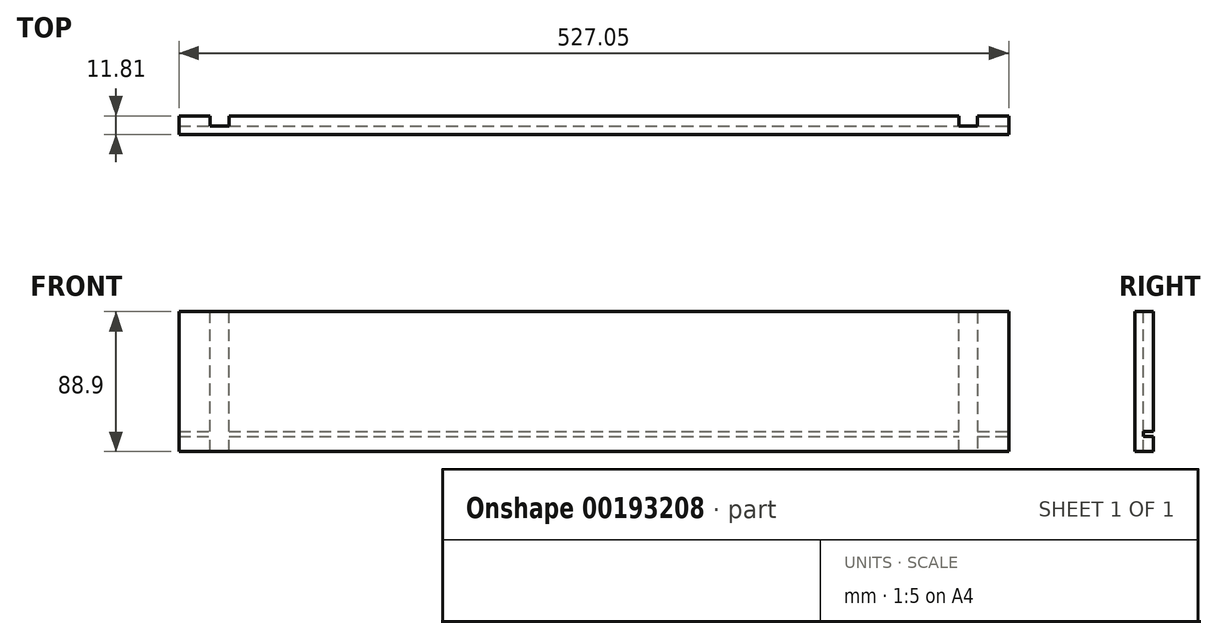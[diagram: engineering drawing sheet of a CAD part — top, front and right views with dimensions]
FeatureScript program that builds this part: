
annotation { "Feature Type Name" : "Feature", "Feature Type Description" : "" }
export const myFeature = defineFeature(function(context is Context, id is Id, definition is map)
    precondition{}
    {
        {
            var Q0;
            Q0=qCreatedBy(makeId("Right.planeOp"),FACE);
            var sketch = newSketch(context, id + "F0", { "sketchPlane" : qUnion([Q0])});
            skLineSegment(sketch, "E0.MirrorCS", {"start": v(12.46, -79.46) * mm, "end": v(12.46, -88.99) * mm});
            skLineSegment(sketch, "E1.MirrorCS", {"start": v(6.1, -76.29) * mm, "end": v(6.1, -79.46) * mm});
            skLineSegment(sketch, "E2.MirrorCS", {"start": v(12.46, -79.46) * mm, "end": v(6.1, -79.46) * mm});
            skLineSegment(sketch, "E3.MirrorCS", {"start": v(12.46, -76.29) * mm, "end": v(6.1, -76.29) * mm});
            skLineSegment(sketch, "E4.MirrorCS", {"start": v(0.65, -0.09) * mm, "end": v(0.65, -88.99) * mm});
            skLineSegment(sketch, "E5.MirrorCS", {"start": v(12.46, -0.09) * mm, "end": v(12.46, -76.29) * mm});
            skLineSegment(sketch, "E6.MirrorCS", {"start": v(12.46, -0.09) * mm, "end": v(0.65, -0.09) * mm});
            skLineSegment(sketch, "E7.MirrorCS", {"start": v(12.46, -88.99) * mm, "end": v(0.65, -88.99) * mm});
            skSolve(sketch);
        }
        {
            var Q0;
            Q0 = qSketchRegion(id + "F0", true);
            var Q1;
            Q1=sQuery(id+"F0.wireOp",EDGE,"E7.MirrorCS");
            var Q2;
            Q2=sQuery(id+"F0.wireOp",EDGE,"E4.MirrorCS");
            var Q3;
            Q3=sQuery(id+"F0.wireOp",EDGE,"E5.MirrorCS");
            var Q4;
            Q4=sQuery(id+"F0.wireOp",EDGE,"E6.MirrorCS");
            var Q5;
            Q5=sQuery(id+"F0.wireOp",EDGE,"E0.MirrorCS");
            var Q6;
            Q6=sQuery(id+"F0.wireOp",EDGE,"E0.MirrorCS");
            var Q7;
            Q7=sQuery(id+"F0.wireOp",EDGE,"E4.MirrorCS");
            var Q8;
            Q8=sQuery(id+"F0.wireOp",EDGE,"E5.MirrorCS");
            var Q9;
            Q9=sQuery(id+"F0.wireOp",EDGE,"E6.MirrorCS");
            var Q10;
            Q10=sQuery(id+"F0.wireOp",EDGE,"E7.MirrorCS");
            var Q11;
            Q11=sQuery(id+"F0.wireOp",EDGE,"E1.MirrorCS");
            var Q12;
            Q12=sQuery(id+"F0.wireOp",EDGE,"E3.MirrorCS");
            var Q13;
            Q13=sQuery(id+"F0.wireOp",EDGE,"E2.MirrorCS");
            var Q14;
            Q14=sQuery(id+"F0.wireOp",EDGE,"E2.MirrorCS");
            var Q15;
            Q15=sQuery(id+"F0.wireOp",EDGE,"E3.MirrorCS");
            var Q16;
            Q16=sQuery(id+"F0.wireOp",EDGE,"E1.MirrorCS");
            extrude(context, id + "F1", {"entities" : qUnion([Q0]), "surfaceEntities" : qUnion([Q1, Q2, Q3, Q4, Q5, Q6, Q7, Q8, Q9, Q10, Q11, Q12, Q13, Q14, Q15, Q16]), "oppositeDirection" : true, "depth" : 527.05 * mm});
        }
        {
            var Q0;
            Q0=qCreatedBy(makeId("Top.planeOp"),FACE);
            var sketch = newSketch(context, id + "F2", { "sketchPlane" : qUnion([Q0])});
            skLineSegment(sketch, "E8.bottom", {"start": v(-31.75, 12.45) * mm, "end": v(-19.91, 12.45) * mm});
            skLineSegment(sketch, "E8.top", {"start": v(-31.75, 6.1) * mm, "end": v(-19.91, 6.1) * mm});
            skLineSegment(sketch, "E8.left", {"start": v(-31.75, 12.45) * mm, "end": v(-31.75, 6.1) * mm});
            skLineSegment(sketch, "E8.right", {"start": v(-19.91, 12.45) * mm, "end": v(-19.91, 6.1) * mm});
            skSolve(sketch);
        }
        {
            var Q0;
            Q0=makeQuery(id+"F1.opExtrude","SWEPT_FACE",FACE,{"disambiguationData":[OSD([sQuery(id+"F0.wireOp",EDGE,"E6.MirrorCS")])]});
            var sketch = newSketch(context, id + "F3", { "sketchPlane" : qUnion([Q0])});
            skLineSegment(sketch, "E9.bottom", {"start": v(-507.14, 12.46) * mm, "end": v(-495.3, 12.46) * mm});
            skLineSegment(sketch, "E9.top", {"start": v(-507.14, 6.1) * mm, "end": v(-495.3, 6.1) * mm});
            skLineSegment(sketch, "E9.left", {"start": v(-507.14, 12.46) * mm, "end": v(-507.14, 6.1) * mm});
            skLineSegment(sketch, "E9.right", {"start": v(-495.3, 12.46) * mm, "end": v(-495.3, 6.1) * mm});
            skSolve(sketch);
        }
        {
            var Q0;
            Q0 = qSketchRegion(id + "F2", true);
            var Q1;
            Q1 = qSketchRegion(id + "F3", true);
            extrude(context, id + "F4", {"entities" : qUnion([Q0, Q1]), "operationType" : NewBodyOperationType.REMOVE, "endBound" : BoundingType.THROUGH_ALL, "oppositeDirection" : true, "depth" : 25.4 * mm});
        }
    });
